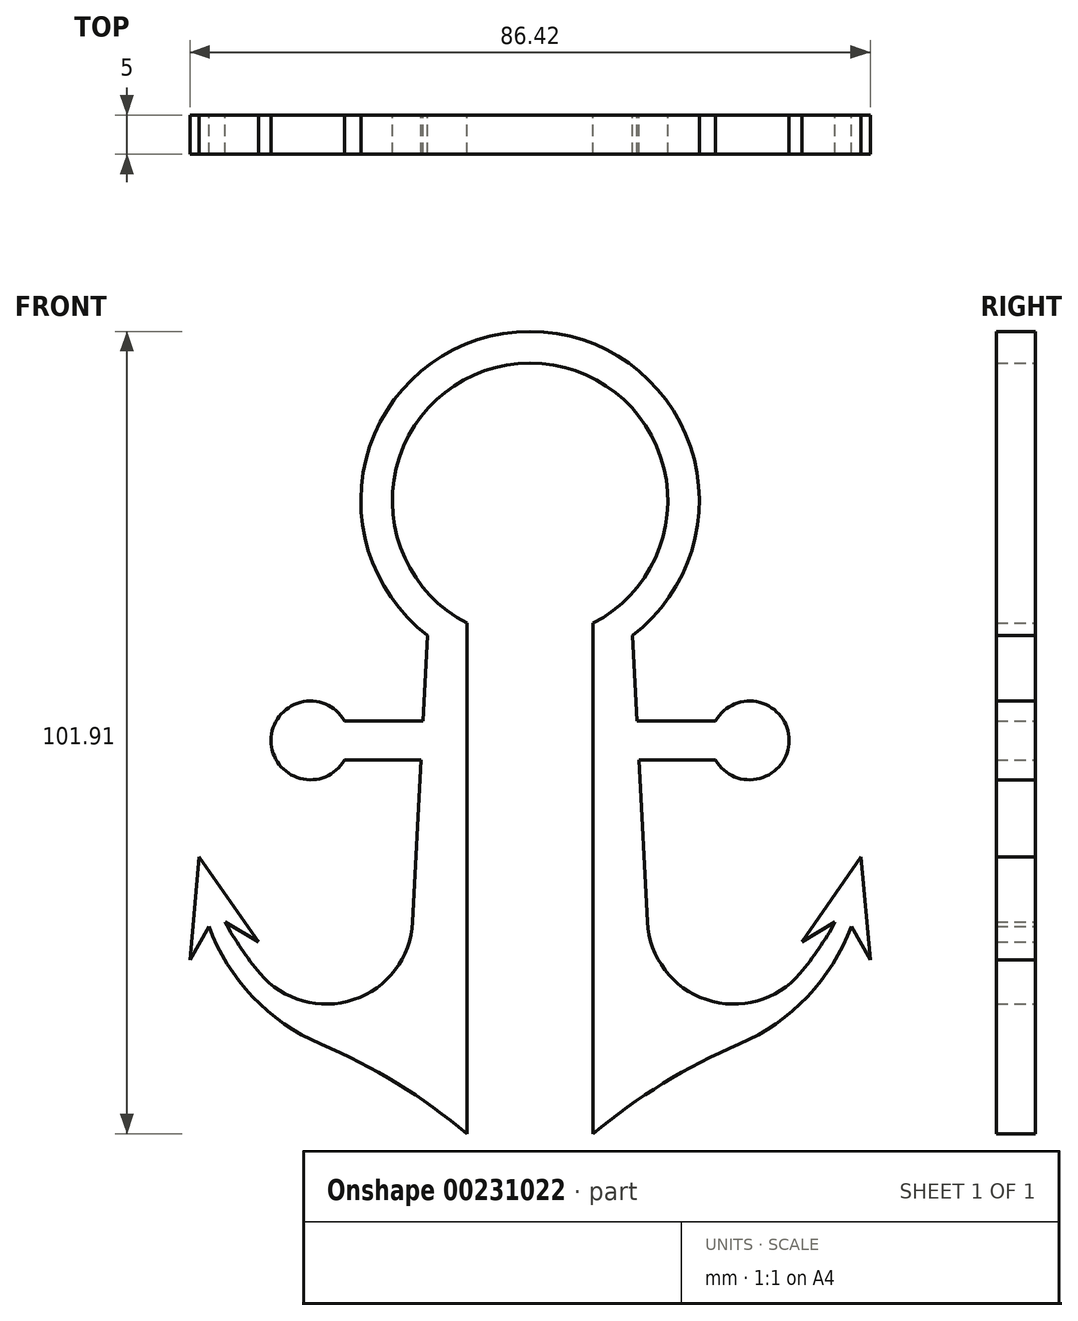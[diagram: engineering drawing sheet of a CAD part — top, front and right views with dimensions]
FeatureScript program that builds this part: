
annotation { "Feature Type Name" : "Feature", "Feature Type Description" : "" }
export const myFeature = defineFeature(function(context is Context, id is Id, definition is map)
    precondition{}
    {
        {
            var Q0;
            Q0=qCreatedBy(makeId("Front.planeOp"),FACE);
            var sketch = newSketch(context, id + "F0", { "sketchPlane" : qUnion([Q0])});
            skCircle(sketch, "E0", {"center": v(0, 0) * mm, "radius": 21.5 * mm, "construction": true});
            skArc(sketch, "E1", {"start": v(0, 21.5) * mm, "mid": v(-20.38, 6.86) * mm, "end": v(-13, -17.12) * mm});
            skLineSegment(sketch, "E2", {"start": v(-8, -19.96) * mm, "end": v(-8, -80.4) * mm});
            skLineSegment(sketch, "E3", {"start": v(-13, -17.12) * mm, "end": v(-13.57, -27.96) * mm});
            skLineSegment(sketch, "E4", {"start": v(-13.57, -27.96) * mm, "end": v(-23.57, -27.96) * mm});
            skArc(sketch, "E5", {"start": v(-23.57, -27.96) * mm, "mid": v(-32.9, -30.46) * mm, "end": v(-23.57, -32.96) * mm});
            skLineSegment(sketch, "E6", {"start": v(-23.57, -32.96) * mm, "end": v(-13.83, -32.96) * mm});
            skLineSegment(sketch, "E7", {"start": v(-13.83, -32.96) * mm, "end": v(-14.9, -53.53) * mm});
            skLineSegment(sketch, "E8", {"start": v(-13.83, -32.96) * mm, "end": v(-13.57, -27.96) * mm, "construction": true});
            skLineSegment(sketch, "E9", {"start": v(-38.74, -53.53) * mm, "end": v(-34.51, -56.05) * mm});
            skLineSegment(sketch, "E10", {"start": v(-34.51, -56.05) * mm, "end": v(-42.04, -45.26) * mm});
            skLineSegment(sketch, "E11", {"start": v(-42.04, -45.26) * mm, "end": v(-43.2, -58.36) * mm});
            skLineSegment(sketch, "E12", {"start": v(-43.2, -58.36) * mm, "end": v(-40.8, -54.07) * mm});
            skArc(sketch, "E13", {"start": v(-40.8, -54.07) * mm, "mid": v(-35.24, -63.02) * mm, "end": v(-26.6, -69.02) * mm});
            skArc(sketch, "E14", {"start": v(-8, -80.4) * mm, "mid": v(-16.88, -74.04) * mm, "end": v(-26.6, -69.02) * mm});
            skLineSegment(sketch, "E15", {"start": v(-40.8, -54.07) * mm, "end": v(-38.74, -53.53) * mm, "construction": true});
            skLineSegment(sketch, "E16", {"start": v(-42.04, -45.26) * mm, "end": v(-39.77, -53.8) * mm, "construction": true});
            skArc(sketch, "E17", {"start": v(-34.3, -60.04) * mm, "mid": v(-22.39, -63.38) * mm, "end": v(-14.9, -53.53) * mm});
            skArc(sketch, "E18", {"start": v(-38.74, -53.53) * mm, "mid": v(-36.69, -56.9) * mm, "end": v(-34.3, -60.04) * mm});
            skLineSegment(sketch, "E19", {"start": v(-43.2, -58.36) * mm, "end": v(-34.51, -56.05) * mm, "construction": true});
            skLineSegment(sketch, "E20", {"start": v(-39.77, -53.8) * mm, "end": v(-38.86, -57.2) * mm, "construction": true});
            skLineSegment(sketch, "E21", {"start": v(-8, -19.96) * mm, "end": v(-8, -15.56) * mm});
            skArc(sketch, "E22", {"start": v(0, 17.5) * mm, "mid": v(-17, 4.12) * mm, "end": v(-8, -15.56) * mm});
            skLineSegment(sketch, "E23", {"start": v(0, 17.5) * mm, "end": v(0, 21.5) * mm});
            skSolve(sketch);
        }
        {
            var Q0;
            Q0 = qSketchRegion(id + "F0", true);
            extrude(context, id + "F1", {"entities" : qUnion([Q0]), "depth" : 5 * mm});
        }
        {
            var Q0;
            Q0=makeQuery(id+"F1.opExtrude","SWEPT_BODY",BODY,{"disambiguationData":[OSD([sQuery(id+"F0.wireOp",EDGE,"E1"),sQuery(id+"F0.wireOp",EDGE,"E2"),sQuery(id+"F0.wireOp",EDGE,"E3"),sQuery(id+"F0.wireOp",EDGE,"E4"),sQuery(id+"F0.wireOp",EDGE,"E5"),sQuery(id+"F0.wireOp",EDGE,"E6"),sQuery(id+"F0.wireOp",EDGE,"E7"),sQuery(id+"F0.wireOp",EDGE,"E9"),sQuery(id+"F0.wireOp",EDGE,"E10"),sQuery(id+"F0.wireOp",EDGE,"E11"),sQuery(id+"F0.wireOp",EDGE,"E12"),sQuery(id+"F0.wireOp",EDGE,"E13"),sQuery(id+"F0.wireOp",EDGE,"E14"),sQuery(id+"F0.wireOp",EDGE,"E17"),sQuery(id+"F0.wireOp",EDGE,"E18"),sQuery(id+"F0.wireOp",EDGE,"E21"),sQuery(id+"F0.wireOp",EDGE,"E22"),sQuery(id+"F0.wireOp",EDGE,"E23")])]});
            var Q1;
            Q1=makeQuery(id+"F1.opExtrude","SWEPT_FACE",FACE,{"disambiguationData":[OSD([sQuery(id+"F0.wireOp",EDGE,"E23")])]});
            mirror(context, id + "F2", {"operationType" : NewBodyOperationType.ADD, "entities" : qUnion([Q0]), "mirrorPlane" : qUnion([Q1])});
        }
    });
